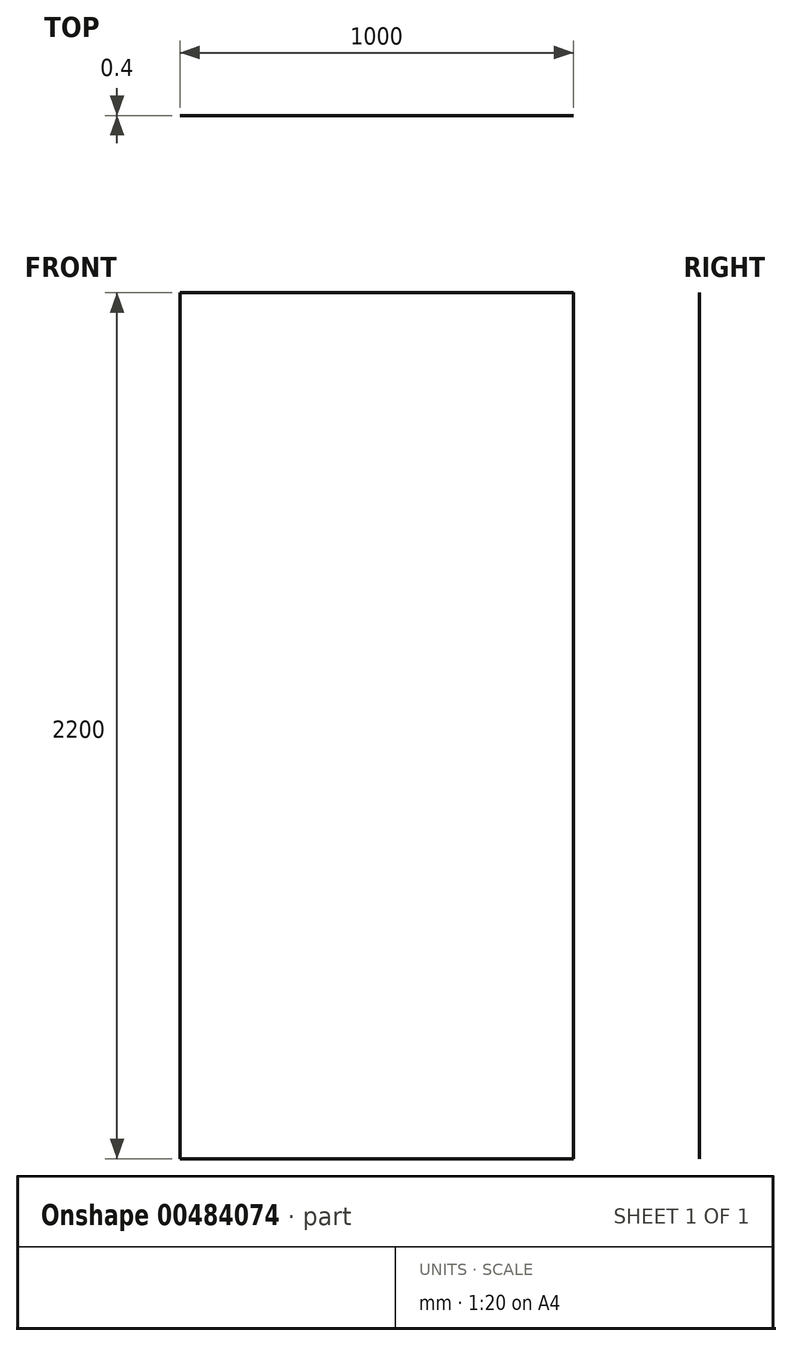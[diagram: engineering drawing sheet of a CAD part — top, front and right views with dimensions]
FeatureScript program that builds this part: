
annotation { "Feature Type Name" : "Feature", "Feature Type Description" : "" }
export const myFeature = defineFeature(function(context is Context, id is Id, definition is map)
    precondition{}
    {
        {
            var Q0;
            Q0=qCreatedBy(makeId("Top.planeOp"),FACE);
            var sketch = newSketch(context, id + "F0", { "sketchPlane" : qUnion([Q0])});
            skLineSegment(sketch, "E0.bottom", {"start": v(0, 0) * mm, "end": v(1000, 0) * mm});
            skLineSegment(sketch, "E0.top", {"start": v(0, -0.4) * mm, "end": v(1000, -0.4) * mm});
            skLineSegment(sketch, "E0.left", {"start": v(0, 0) * mm, "end": v(0, -0.4) * mm});
            skLineSegment(sketch, "E0.right", {"start": v(1000, 0) * mm, "end": v(1000, -0.4) * mm});
            skSolve(sketch);
        }
        {
            var Q0;
            Q0=makeQuery(id+"F0.imprint","IMPRINT",FACE,{"disambiguationData":[TD([[makeQuery(id+"F0.imprint","IMPRINT",EDGE,{"derivedFrom":sQuery(id+"F0.wireOp",EDGE,"E0.top")}),1.0]])]});
            extrude(context, id + "F1", {"entities" : qUnion([Q0]), "depth" : 2200 * mm});
        }
    });
